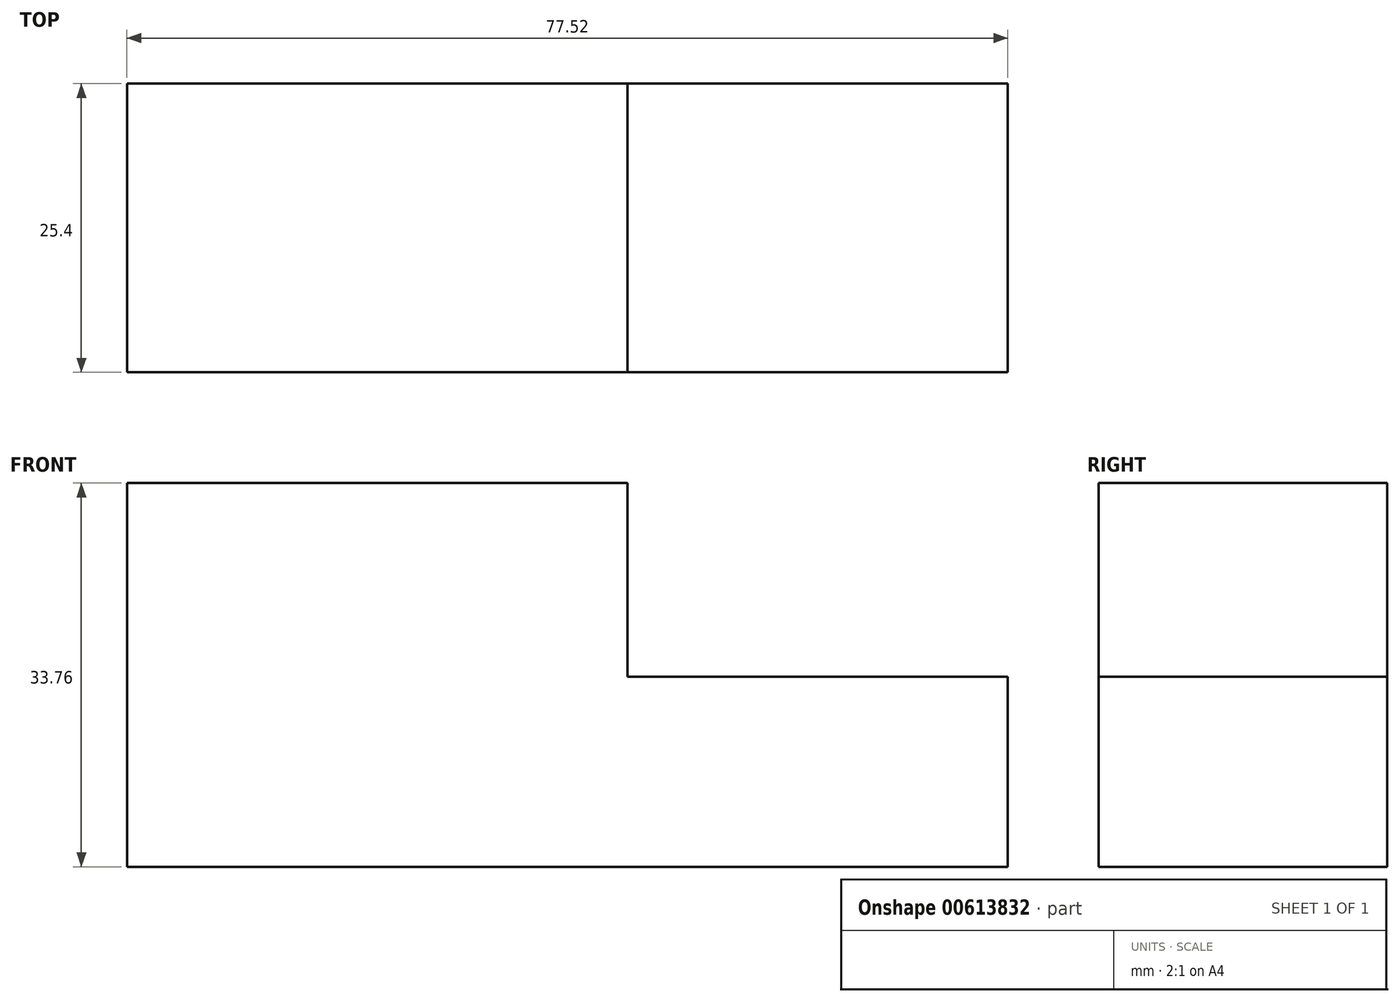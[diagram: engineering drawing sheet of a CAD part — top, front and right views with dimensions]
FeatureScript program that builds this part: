
annotation { "Feature Type Name" : "Feature", "Feature Type Description" : "" }
export const myFeature = defineFeature(function(context is Context, id is Id, definition is map)
    precondition{}
    {
        {
            var Q0;
            Q0=qCreatedBy(makeId("Front.planeOp"),FACE);
            var sketch = newSketch(context, id + "F0", { "sketchPlane" : qUnion([Q0])});
            skLineSegment(sketch, "E0", {"start": v(-75.02, 39.05) * mm, "end": v(-30.98, 39.05) * mm});
            skLineSegment(sketch, "E1", {"start": v(-30.98, 39.05) * mm, "end": v(-30.98, 22.02) * mm});
            skLineSegment(sketch, "E2", {"start": v(-30.98, 22.02) * mm, "end": v(2.5, 22.02) * mm});
            skLineSegment(sketch, "E3", {"start": v(2.5, 22.02) * mm, "end": v(2.5, 5.29) * mm});
            skLineSegment(sketch, "E4", {"start": v(2.5, 5.29) * mm, "end": v(-75.02, 5.29) * mm});
            skLineSegment(sketch, "E5", {"start": v(-75.02, 5.29) * mm, "end": v(-75.02, 39.05) * mm});
            skSolve(sketch);
        }
        {
            var Q0;
            Q0 = qSketchRegion(id + "F0", true);
            extrude(context, id + "F1", {"entities" : qUnion([Q0]), "depth" : 25.4 * mm, "offsetDistance" : 25.4 * mm});
        }
    });
